# Revit family: Sandkasse_komplett_Default
name_source: partatom
category: Generic Models
units: mm (PartAtom-declared; Revit-internal decimal feet)

## family parameters
Always vertical = Yes
Can host rebar = No
Cut with Voids When Loaded = No
Part Type = Normal
Room Calculation Point = No
Round Connector Dimension = Use Diameter
Shared = No
Work Plane-Based = No

## types (1)
- Type 1
    Artnr = 61-200-190
    Artnr_Default = 61-200-190
    CheckedDate = -
    CheckedDate_Default = -
    Default Elevation = 0 mm  [stored 0 ft]
    Description = Sandkasse_komplett
    Description_Default = Sandkasse_komplett
    Number = 74923
    Number_Default = 74923
    PartName = Sandkasse_komplett
    PartName_Default = Sandkasse_komplett
    Revision = 0
    Revision_Default = 0
    Weight_Default = 17142890.36

note: [stored X ft] marks values corroborated as IEEE doubles in the binary element streams (Revit-internal decimal feet)

## geometry (parser evidence)
native form markers: Sweep x12
no freeform markers — native parametric forms only
